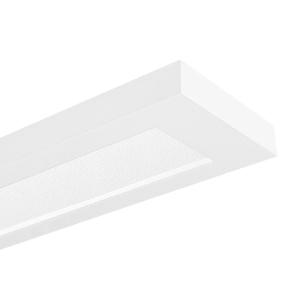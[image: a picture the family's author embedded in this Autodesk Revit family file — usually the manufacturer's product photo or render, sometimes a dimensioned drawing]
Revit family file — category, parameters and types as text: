
# Revit family: 3f_filippi_-_3f_travetta_di_lgs_3f_filippi_-_11632_-_3f_trav__led_di_2x22w-940_dali_lgs_l1590_923d
name_source: partatom
category: Lighting Fixtures
units: mm (PartAtom-declared; Revit-internal decimal feet)

## family parameters
Cut with Voids When Loaded = No
Host = Face
Light Source = No
Part Type = Normal
Room Calculation Point = No
Round Connector Dimension = Use Diameter
Shared = No

## types (1)
- 3F Filippi - 3F Travetta DI LGS (1 x LED, 3950 lm, 49 W, 4000 K)
    Apparent Load = 49 VA
    Approval mark = ENEC
    CIE Flux Codes = 64 93 99 85 100
    Color Rendering = 90
    Color Temperature = 4000 K
    Control Gear = Electronic transformer
    Default Elevation = 1800 mm
    Description = ILLUMINOTECHNICAL
Luminous efficiency 100% (DLOR 85%, ULOR 15%).
Initial luminous flux of the luminaire 3950 lm.
Symmetric direct-indirect distribution.
Installation Interdistance Transv.D = 1.18 x hu - Long.D = 1.18 x hu.
Average luminance <3000 cd/m² for radial angles >65°.
Tabular UGR (CIE 117 - 4H-8H; S=0.25H; 70/50/20): RUG 16.4 - 16.9.
Beam angle: 89° - 91°.
Luminous efficacy 81 lm/W.
Lifetime (L93/B10): 30000 h. (tq+25°C)
Lifetime (L90/B10): 50000 h. (tq+25°C)
Lifetime (L85/B10): 80000 h. (tq+25°C)
Lifetime (L80/B10): 100000 h. (tq+25°C)
Sudden decreased luminous flux after 50000 hours: 0% (C0).
Photobiological safety in compliance with IEC/TR 62778: RG0 risk exempt, (IEC 62471).
In compliance with IEC/EN 62722-2-1 - IEC/EN 62717 standards.

SOURCE
2 linear LED modules 22W/940.
Energy efficiency class (UE 2019/2020 - UE 2019/2015): E.
CIE 13.3 Colour rendering index: CRI >90 (R9 >50%).
IES TM-30 Fidelity Index: Rf = 92 Rg = 101.
CCT nominal colour temperature 4000 K.
Colour initial tolerance (MacAdam): SDCM 2.

MECHANICAL
Housing with squared shape in white painted galvannealed steel, with nonreflecting surface.
Flow recuperator in semi-glossy aluminium.
LGS micro-prismatic flat diffuser in transparent methacrylate (PMMA), multi-lenticular exterior, anti-glare.
Anti-glare opal polycarbonate filter for brightness uniformity.
Upper holes closing film made of opal polycarbonate.
Luminaire with limited surface temperature. - D - (EN 60598-2-24)
Dimensions: 1590x190 mm, height 60 mm. Weight 5.6 kg.
IP20 protection degree.
Glow-wire test resistance 650°C.

ELECTRICAL
Halogen Free DALI-2 DATI (Parts 251, 252, 253), PUSH-DIM, electronic wiring 230V-50/60Hz, power factor 0.95 at full load, THD <25%, constant output current, SELV, class I, 1 driver, 1 DALI addresse.
Power of the luminaire 49 W.
CE - IEC 60598-1 - EN 60598-1.
SAFE FLICKER: PstLM=<1 and SVM=<0.4 (IEC TR 61547-1 and IEC TR 63158), to ensure a more comfortable and safe light.
Luminaire compliant with EN 60598-2-22 for power supply from a centralised emergency system CPSS (Central Power Supply System), not incorporated in the luminaire - high risk areas excluded. The default power and flux are 100% in AC and 15% in DC.
Ambient temperature from 0°C to +25°C.
Temperature class T6 max 85°C.
Relative humidity UR: <85%.

INSTALLATION
Suspended.
All accessories dedicated to this product are available on the Catalog and on our website www.3F-Filippi.com.

APPLICATIONS
In environments, even with reduced height, requiring a comfortable light.
In environments with VDTs, managerial offices and staterooms, public offices and schools.

LIGHT MANAGEMENT
Recommended minimum setting: 10%.
The luminaire, equipped with (DALI-2 DATI) driver, can be controlled manually with 3F Easy Dim technology or automatically/manually with wired or wireless DALI/D2D control systems.
The D2D driver guarantees interoperability with other devices with the same certification by making the following information available:
Device Data (Part 251), Energy Report (Part 252), Diagnosis & Maintenance (Part 253).
In electrical systems without a regulation system (manual or automatic) and DALI bus, a suitable jumper must be made on the DA-DA terminals of the appliance.

WARNING
Luminaire designed for disposal/recycling at end-of-life.
Replaceable (LED only) light source by a professional. Replaceable control gear by a professional.
    Height = 60 mm  [stored 0.19685 ft]
    Lamp = 1 x LED
    Lamp Light Flux = 3950 lm
    Lamp Power = 49 W
    Lamp count = 1
    Length = 1590 mm
    Lifetime = 50000 h
    Luminous efficacy = 81 lm/W
    Manufacturer = 3F Filippi
    ModVariant = No
    Model = 3F Filippi - 11632 - 3F Trav. LED DI 2x22W-940 DALI LGS L1590
    Mounting Place = Ceiling
    Mounting Type = Pendant
    Number of Poles = 1
    OnlyDefault = Yes
    Power Factor = 1
    Product Name = 3F Filippi - 3F Travetta DI LGS
    Product group = pendant luminaire
    ProductGroupID = 9
    Protection Class = Protection class I
    Protection Degree = IP 20
    RLX_Detail_Level = 1
    RLX_Emergency_Light_Flux = 0 lm
    RLX_Emergency_Type = 0
    RLX_Emergency_Type_DB = No
    RlxData = <blob elided: 52689 chars, md5=ebf76f05>
    Socket = socket
    Standby Power = 0 W
    System Light Flux = 3950 lm
    System Power = 49 W
    Type Comments = Product without accessories
    Type Image = 3ffilippi_3f_travetta_led_lgs.jpg
    URL = http://relux.com
    VarID = ---
    Voltage = 0 V
    Weight = 0.00 kg
    Width = 190 mm  [stored 0.62336 ft]

note: [stored X ft] marks values corroborated as IEEE doubles in the binary element streams (Revit-internal decimal feet)

## geometry (parser evidence)
native form markers: Blend x4, Sweep x13
no freeform markers — native parametric forms only
